# Revit family: Seitenhalter - SH M10 FS, FT, A4
name_source: partatom
category: Generic Models
revit_build: Autodesk Revit 2017 (Build: 20190508_0315(x64)
units: mm (PartAtom-declared; Revit-internal decimal feet)

## family parameters
Always vertical = Yes
Can host rebar = No
Cut with Voids When Loaded = No
Part Type = Normal
Room Calculation Point = No
Round Connector Dimension = Use Diameter
Shared = No
Work Plane-Based = No

## types (3) — shared parameters
Height = 58 mm  [stored 0.190289 ft]
Manufacturer = OBO Bettermann
URL = http://www.obo-bettermann.com

## per-type parameters (varying)
| type | GTIN | Manufacturer Art.No. | Material | Width |
| SH M10 FS | 4012196608539 | 6015336 | Strip-galvanised | 58 mm  [stored 0.190289 ft] |
| SH M10 FT | 4012196951970 | 6015338 | Hot-dip galvanised | 58 mm  [stored 0.190289 ft] |
| SH M10 A4 | 4012196952038 | 6015340 | Stainless steel, grade 316 | 30 mm  [stored 0.0984252 ft] |

note: column(s) folded — value = type name in every type: Article Type

note: [stored X ft] marks values corroborated as IEEE doubles in the binary element streams (Revit-internal decimal feet)

## geometry (parser evidence)
native form markers: Sweep x2
no freeform markers — native parametric forms only
